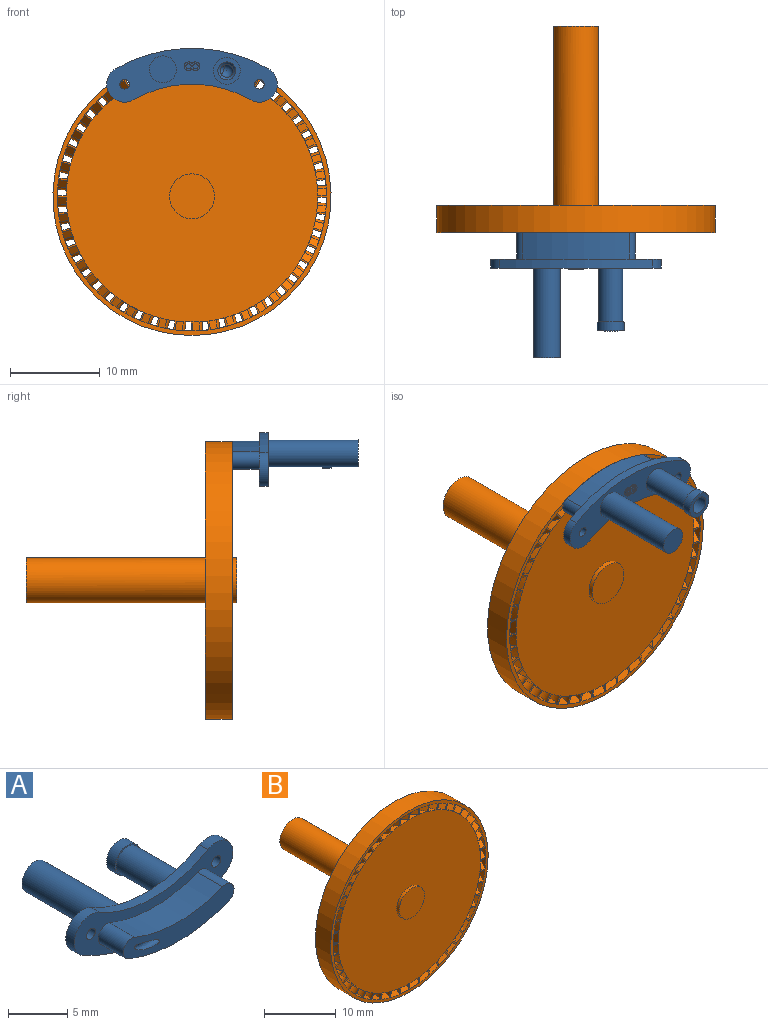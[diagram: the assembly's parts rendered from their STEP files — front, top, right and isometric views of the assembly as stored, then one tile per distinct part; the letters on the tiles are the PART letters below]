
ASSEMBLY  parts=2 mates=1
PART A: 33 faces, bbox 19x14.8x6 mm
  f0: cylinder r=1.5mm len=10mm, axis (0,-1,0), area 94.2mm2, adj f12,f18
  f1: cone r=0.4mm half-angle=45deg, axis (0,1,0), area 2.1mm2, adj f4,f19
  f2: cylinder r=1mm len=3mm, axis (0,1,0), area 9.4mm2, adj f9,f15,f16,f17
  f3: cylinder r=1mm len=3mm, axis (0,1,0), area 9.4mm2, adj f9,f15,f16,f17
  f4: cylinder r=1mm len=6.4mm, axis (0,-1,0), area 40.2mm2, adj f1,f13
  f5: cylinder r=1.5mm len=3mm, axis (0,-1,0), area 9.4mm2, adj f13,f14
  f6: cylinder r=1.35mm len=6mm, axis (0,-1,0), area 50.9mm2, adj f12,f14
  f7: cylinder r=13mm len=13mm, axis (0,-1,0), area 13.6mm2, adj f9,f10,f11,f12
  f8: cylinder r=17mm len=17mm, axis (0,-1,0), area 17.8mm2, adj f9,f10,f11,f12
  f9: plane 19x6.01mm, normal (0,-1,0), area 47.4mm2, adj f2,f3,f7,f8,f10,f11,f15,f16
  f10: cylinder r=2mm len=3.73mm, axis (0,-1,0), area 6.3mm2, adj f7,f8,f9,f12
  f11: cylinder r=2mm len=3.73mm, axis (0,-1,0), area 6.3mm2, adj f7,f8,f9,f12
  f12: plane 19x6.01mm, normal (0,1,0), area 59.4mm2, adj f0,f6,f7,f8,f10,f11,f24,f25
  f13: plane 3x3mm, normal (0,1,0), area 3.9mm2, adj f4,f5
  f14: plane 3x3mm, normal (0,-1,0), area 1.3mm2, adj f5,f6
  f15: cylinder r=16mm len=11.99mm, axis (0,1,0), area 36.9mm2, adj f2,f3,f9,f17
  f16: cylinder r=14mm len=10.49mm, axis (0,1,0), area 32.3mm2, adj f2,f3,f9,f17
  f17: plane 13.24x3.09mm, normal (0,-1,0), area 24.3mm2, adj f2,f3,f15,f16,f21
  f18: plane 3x3mm, normal (0,1,0), area 7.1mm2, adj f0
  f19: cylinder r=0.73mm len=2.27mm, axis (0,-1,0), area 9.9mm2, adj f1,f20,f23
  f20: sphere r=0.73mm, area 2.6mm2, adj f19,f22
  f21: bspline ~8.77x3.01mm, area 17.2mm2, adj f17,f22,f23
  f22: bspline ~1.05x0.66mm, area 0.6mm2, adj f20,f21,f23
  f23: bspline ~0.97x0.73mm, area 0.7mm2, adj f19,f21,f22
  f24: cylinder r=0.53mm len=1.07mm, axis (0,-1,0), area 3.4mm2, adj f9,f12
  f25: cylinder r=0.53mm len=1.07mm, axis (0,-1,0), area 3.4mm2, adj f9,f12
  f26: cylinder r=0.49mm len=0.97mm, axis (0,-1,0), area 0.5mm2, adj f12,f29,f30
  f27: cylinder r=0.29mm len=0.58mm, axis (0,-1,0), area 0.4mm2, adj f30,f32
  f28: cylinder r=0.29mm len=0.58mm, axis (0,-1,0), area 0.4mm2, adj f30,f31
  f29: cylinder r=0.49mm len=0.97mm, axis (0,-1,0), area 0.5mm2, adj f12,f26,f30
  f30: plane 1.75x0.97mm, normal (0,1,0), area 0.9mm2, adj f26,f27,f28,f29
  f31: plane 0.58x0.58mm, normal (0,1,0), area 0.3mm2, adj f28
  f32: plane 0.58x0.58mm, normal (0,1,0), area 0.3mm2, adj f27
PART B: 295 faces, bbox 31x23.5x31 mm
  f0: cylinder r=2.02mm len=3mm, axis (0,0,-1), area 3.4mm2, adj f192,f240,f241,f289
  f1: plane 1.03x0.8mm, normal (-0.71,0.7,0), area 1.1mm2, adj f2,f239,f240,f242
  f2: cylinder r=1mm len=1.4mm, axis (0,0,-1), area 1.6mm2, adj f1,f3,f239,f242
  f3: plane 1.03x0.8mm, normal (-0.72,-0.7,0), area 1.1mm2, adj f2,f239,f241,f242
  f4: cylinder r=2.02mm len=3mm, axis (0.13,0,-0.99), area 3.4mm2, adj f239,f240,f241,f242
  f5: plane 1.12x0.91mm, normal (-0.7,0.7,-0.09), area 1.1mm2, adj f6,f238,f240,f243
  f6: cylinder r=1mm len=1.4mm, axis (0.13,0,-0.99), area 1.6mm2, adj f5,f7,f238,f243
  f7: plane 1.12x0.9mm, normal (-0.71,-0.7,-0.09), area 1.1mm2, adj f6,f238,f241,f243
  f8: cylinder r=2.02mm len=3mm, axis (0.26,0,-0.97), area 3.4mm2, adj f238,f240,f241,f243
  f9: plane 1.2x1.01mm, normal (-0.69,0.7,-0.18), area 1.1mm2, adj f10,f237,f240,f244
  f10: cylinder r=1mm len=1.4mm, axis (0.26,0,-0.97), area 1.6mm2, adj f9,f11,f237,f244
  f11: plane 1.19x1.01mm, normal (-0.69,-0.7,-0.19), area 1.1mm2, adj f10,f237,f241,f244
  f12: cylinder r=2.02mm len=3mm, axis (0.38,0,-0.92), area 3.4mm2, adj f237,f240,f241,f244
  f13: plane 1.25x1.1mm, normal (-0.66,0.7,-0.27), area 1.1mm2, adj f14,f236,f240,f245
  f14: cylinder r=1mm len=1.4mm, axis (0.38,0,-0.92), area 1.6mm2, adj f13,f15,f236,f245
  f15: plane 1.25x1.1mm, normal (-0.66,-0.7,-0.27), area 1.1mm2, adj f14,f236,f241,f245
  f16: cylinder r=2.02mm len=3mm, axis (0.5,0,-0.87), area 3.4mm2, adj f236,f240,f241,f245
  f17: plane 1.28x1.17mm, normal (-0.62,0.7,-0.36), area 1.1mm2, adj f18,f235,f240,f246
  f18: cylinder r=1mm len=1.4mm, axis (0.5,0,-0.87), area 1.6mm2, adj f17,f19,f235,f246
  f19: plane 1.28x1.16mm, normal (-0.62,-0.7,-0.36), area 1.1mm2, adj f18,f235,f241,f246
  f20: cylinder r=2.02mm len=3mm, axis (0.61,0,-0.79), area 3.4mm2, adj f235,f240,f241,f246
  f21: plane 1.29x1.22mm, normal (-0.56,0.7,-0.43), area 1.1mm2, adj f22,f234,f240,f247
  f22: cylinder r=1mm len=1.4mm, axis (0.61,0,-0.79), area 1.6mm2, adj f21,f23,f234,f247
  f23: plane 1.29x1.21mm, normal (-0.57,-0.7,-0.44), area 1.1mm2, adj f22,f234,f241,f247
  f24: cylinder r=2.02mm len=3mm, axis (0.71,0,-0.71), area 3.4mm2, adj f234,f240,f241,f247
  f25: plane 1.28x1.25mm, normal (-0.5,0.7,-0.5), area 1.1mm2, adj f26,f233,f240,f248
  f26: cylinder r=1mm len=1.4mm, axis (0.71,0,-0.71), area 1.6mm2, adj f25,f27,f233,f248
  f27: plane 1.28x1.24mm, normal (-0.51,-0.7,-0.51), area 1.1mm2, adj f26,f233,f241,f248
  f28: cylinder r=2.02mm len=3mm, axis (0.79,0,-0.61), area 3.4mm2, adj f233,f240,f241,f248
  f29: plane 1.25x1.25mm, normal (-0.43,0.7,-0.56), area 1.1mm2, adj f30,f232,f240,f249
  f30: cylinder r=1mm len=1.4mm, axis (0.79,0,-0.61), area 1.6mm2, adj f29,f31,f232,f249
  f31: plane 1.25x1.25mm, normal (-0.44,-0.7,-0.57), area 1.1mm2, adj f30,f232,f241,f249
  f32: cylinder r=2.02mm len=3mm, axis (0.87,0,-0.5), area 3.4mm2, adj f232,f240,f241,f249
  f33: plane 1.24x1.2mm, normal (-0.36,0.7,-0.62), area 1.1mm2, adj f34,f231,f240,f250
  f34: cylinder r=1mm len=1.4mm, axis (0.87,0,-0.5), area 1.6mm2, adj f33,f35,f231,f250
  f35: plane 1.24x1.19mm, normal (-0.36,-0.7,-0.62), area 1.1mm2, adj f34,f231,f241,f250
  f36: cylinder r=2.02mm len=3mm, axis (0.92,0,-0.38), area 3.4mm2, adj f231,f240,f241,f250
  f37: plane 1.2x1.12mm, normal (-0.27,0.7,-0.66), area 1.1mm2, adj f38,f230,f240,f251
  f38: cylinder r=1mm len=1.4mm, axis (0.92,0,-0.38), area 1.6mm2, adj f37,f39,f230,f251
  f39: plane 1.2x1.12mm, normal (-0.27,-0.7,-0.66), area 1.1mm2, adj f38,f230,f241,f251
  f40: cylinder r=2.02mm len=3mm, axis (0.97,0,-0.26), area 3.4mm2, adj f230,f240,f241,f251
  f41: plane 1.15x1.03mm, normal (-0.18,0.7,-0.69), area 1.1mm2, adj f42,f229,f240,f252
  f42: cylinder r=1mm len=1.4mm, axis (0.97,0,-0.26), area 1.6mm2, adj f41,f43,f229,f252
  f43: plane 1.14x1.02mm, normal (-0.19,-0.7,-0.69), area 1.1mm2, adj f42,f229,f241,f252
  f44: cylinder r=2.02mm len=3mm, axis (0.99,0,-0.13), area 3.4mm2, adj f229,f240,f241,f252
  f45: plane 1.07x0.92mm, normal (-0.09,0.7,-0.7), area 1.1mm2, adj f46,f228,f240,f253
  f46: cylinder r=1mm len=1.4mm, axis (0.99,0,-0.13), area 1.6mm2, adj f45,f47,f228,f253
  f47: plane 1.07x0.91mm, normal (-0.09,-0.7,-0.71), area 1.1mm2, adj f46,f228,f241,f253
  f48: cylinder r=2.02mm len=3mm, axis (1,0,0), area 3.4mm2, adj f228,f240,f241,f253
  f49: plane 1.03x0.8mm, normal (0,0.7,-0.71), area 1.1mm2, adj f50,f227,f240,f254
  f50: cylinder r=1mm len=1.4mm, axis (1,0,0), area 1.6mm2, adj f49,f51,f227,f254
  f51: plane 1.03x0.8mm, normal (0,-0.7,-0.72), area 1.1mm2, adj f50,f227,f241,f254
  f52: cylinder r=2.02mm len=3mm, axis (0.99,0,0.13), area 3.4mm2, adj f227,f240,f241,f254
  f53: plane 1.12x0.91mm, normal (0.09,0.7,-0.7), area 1.1mm2, adj f54,f226,f240,f255
  f54: cylinder r=1mm len=1.4mm, axis (0.99,0,0.13), area 1.6mm2, adj f53,f55,f226,f255
  f55: plane 1.12x0.9mm, normal (0.09,-0.7,-0.71), area 1.1mm2, adj f54,f226,f241,f255
  f56: cylinder r=2.02mm len=3mm, axis (0.97,0,0.26), area 3.4mm2, adj f226,f240,f241,f255
  f57: plane 1.2x1.01mm, normal (0.18,0.7,-0.69), area 1.1mm2, adj f58,f225,f240,f256
  f58: cylinder r=1mm len=1.4mm, axis (0.97,0,0.26), area 1.6mm2, adj f57,f59,f225,f256
  f59: plane 1.19x1.01mm, normal (0.19,-0.7,-0.69), area 1.1mm2, adj f58,f225,f241,f256
  f60: cylinder r=2.02mm len=3mm, axis (0.92,0,0.38), area 3.4mm2, adj f225,f240,f241,f256
  f61: plane 1.25x1.1mm, normal (0.27,0.7,-0.66), area 1.1mm2, adj f62,f224,f240,f257
  f62: cylinder r=1mm len=1.4mm, axis (0.92,0,0.38), area 1.6mm2, adj f61,f63,f224,f257
  f63: plane 1.25x1.1mm, normal (0.27,-0.7,-0.66), area 1.1mm2, adj f62,f224,f241,f257
  f64: cylinder r=2.02mm len=3mm, axis (0.87,0,0.5), area 3.4mm2, adj f224,f240,f241,f257
  f65: plane 1.28x1.17mm, normal (0.36,0.7,-0.62), area 1.1mm2, adj f66,f223,f240,f258
  f66: cylinder r=1mm len=1.4mm, axis (0.87,0,0.5), area 1.6mm2, adj f65,f67,f223,f258
  f67: plane 1.28x1.16mm, normal (0.36,-0.7,-0.62), area 1.1mm2, adj f66,f223,f241,f258
  f68: cylinder r=2.02mm len=3mm, axis (0.79,0,0.61), area 3.4mm2, adj f223,f240,f241,f258
  f69: plane 1.29x1.22mm, normal (0.43,0.7,-0.56), area 1.1mm2, adj f70,f222,f240,f259
  f70: cylinder r=1mm len=1.4mm, axis (0.79,0,0.61), area 1.6mm2, adj f69,f71,f222,f259
  f71: plane 1.29x1.21mm, normal (0.44,-0.7,-0.57), area 1.1mm2, adj f70,f222,f241,f259
  f72: cylinder r=2.02mm len=3mm, axis (0.71,0,0.71), area 3.4mm2, adj f222,f240,f241,f259
  f73: plane 1.28x1.25mm, normal (0.5,0.7,-0.5), area 1.1mm2, adj f74,f221,f240,f260
  f74: cylinder r=1mm len=1.4mm, axis (0.71,0,0.71), area 1.6mm2, adj f73,f75,f221,f260
  f75: plane 1.28x1.24mm, normal (0.51,-0.7,-0.51), area 1.1mm2, adj f74,f221,f241,f260
  f76: cylinder r=2.02mm len=3mm, axis (0.61,0,0.79), area 3.4mm2, adj f221,f240,f241,f260
  f77: plane 1.25x1.25mm, normal (0.56,0.7,-0.43), area 1.1mm2, adj f78,f220,f240,f261
  f78: cylinder r=1mm len=1.4mm, axis (0.61,0,0.79), area 1.6mm2, adj f77,f79,f220,f261
  f79: plane 1.25x1.25mm, normal (0.57,-0.7,-0.44), area 1.1mm2, adj f78,f220,f241,f261
  f80: cylinder r=2.02mm len=3mm, axis (0.5,0,0.87), area 3.4mm2, adj f220,f240,f241,f261
  f81: plane 1.24x1.2mm, normal (0.62,0.7,-0.36), area 1.1mm2, adj f82,f219,f240,f262
  f82: cylinder r=1mm len=1.4mm, axis (0.5,0,0.87), area 1.6mm2, adj f81,f83,f219,f262
  f83: plane 1.24x1.19mm, normal (0.62,-0.7,-0.36), area 1.1mm2, adj f82,f219,f241,f262
  f84: cylinder r=2.02mm len=3mm, axis (0.38,0,0.92), area 3.4mm2, adj f219,f240,f241,f262
  f85: plane 1.2x1.12mm, normal (0.66,0.7,-0.27), area 1.1mm2, adj f86,f218,f240,f263
  f86: cylinder r=1mm len=1.4mm, axis (0.38,0,0.92), area 1.6mm2, adj f85,f87,f218,f263
  f87: plane 1.2x1.12mm, normal (0.66,-0.7,-0.27), area 1.1mm2, adj f86,f218,f241,f263
  f88: cylinder r=2.02mm len=3mm, axis (0.26,0,0.97), area 3.4mm2, adj f218,f240,f241,f263
  f89: plane 1.15x1.03mm, normal (0.69,0.7,-0.18), area 1.1mm2, adj f90,f217,f240,f264
  f90: cylinder r=1mm len=1.4mm, axis (0.26,0,0.97), area 1.6mm2, adj f89,f91,f217,f264
  f91: plane 1.14x1.02mm, normal (0.69,-0.7,-0.19), area 1.1mm2, adj f90,f217,f241,f264
  f92: cylinder r=2.02mm len=3mm, axis (0.13,0,0.99), area 3.4mm2, adj f217,f240,f241,f264
  f93: plane 1.07x0.92mm, normal (0.7,0.7,-0.09), area 1.1mm2, adj f94,f216,f240,f265
  f94: cylinder r=1mm len=1.4mm, axis (0.13,0,0.99), area 1.6mm2, adj f93,f95,f216,f265
  f95: plane 1.07x0.91mm, normal (0.71,-0.7,-0.09), area 1.1mm2, adj f94,f216,f241,f265
  f96: cylinder r=2.02mm len=3mm, axis (0,0,1), area 3.4mm2, adj f216,f240,f241,f265
  f97: plane 1.03x0.8mm, normal (0.71,0.7,0), area 1.1mm2, adj f98,f215,f240,f266
  f98: cylinder r=1mm len=1.4mm, axis (0,0,1), area 1.6mm2, adj f97,f99,f215,f266
  f99: plane 1.03x0.8mm, normal (0.72,-0.7,0), area 1.1mm2, adj f98,f215,f241,f266
  f100: cylinder r=2.02mm len=3mm, axis (-0.13,0,0.99), area 3.4mm2, adj f215,f240,f241,f266
  f101: plane 1.12x0.91mm, normal (0.7,0.7,0.09), area 1.1mm2, adj f102,f214,f240,f267
  f102: cylinder r=1mm len=1.4mm, axis (-0.13,0,0.99), area 1.6mm2, adj f101,f103,f214,f267
  f103: plane 1.12x0.9mm, normal (0.71,-0.7,0.09), area 1.1mm2, adj f102,f214,f241,f267
  f104: cylinder r=2.02mm len=3mm, axis (-0.26,0,0.97), area 3.4mm2, adj f214,f240,f241,f267
  f105: plane 1.2x1.01mm, normal (0.69,0.7,0.18), area 1.1mm2, adj f106,f213,f240,f268
  f106: cylinder r=1mm len=1.4mm, axis (-0.26,0,0.97), area 1.6mm2, adj f105,f107,f213,f268
  f107: plane 1.19x1.01mm, normal (0.69,-0.7,0.19), area 1.1mm2, adj f106,f213,f241,f268
  f108: cylinder r=2.02mm len=3mm, axis (-0.38,0,0.92), area 3.4mm2, adj f213,f240,f241,f268
  f109: plane 1.25x1.1mm, normal (0.66,0.7,0.27), area 1.1mm2, adj f110,f212,f240,f269
  f110: cylinder r=1mm len=1.4mm, axis (-0.38,0,0.92), area 1.6mm2, adj f109,f111,f212,f269
  f111: plane 1.25x1.1mm, normal (0.66,-0.7,0.27), area 1.1mm2, adj f110,f212,f241,f269
  f112: cylinder r=2.02mm len=3mm, axis (-0.5,0,0.87), area 3.4mm2, adj f212,f240,f241,f269
  f113: plane 1.28x1.17mm, normal (0.62,0.7,0.36), area 1.1mm2, adj f114,f211,f240,f270
  f114: cylinder r=1mm len=1.4mm, axis (-0.5,0,0.87), area 1.6mm2, adj f113,f115,f211,f270
  f115: plane 1.28x1.16mm, normal (0.62,-0.7,0.36), area 1.1mm2, adj f114,f211,f241,f270
  f116: cylinder r=2.02mm len=3mm, axis (-0.61,0,0.79), area 3.4mm2, adj f211,f240,f241,f270
  f117: plane 1.29x1.22mm, normal (0.56,0.7,0.43), area 1.1mm2, adj f118,f210,f240,f271
  f118: cylinder r=1mm len=1.4mm, axis (-0.61,0,0.79), area 1.6mm2, adj f117,f119,f210,f271
  f119: plane 1.29x1.21mm, normal (0.57,-0.7,0.44), area 1.1mm2, adj f118,f210,f241,f271
  f120: cylinder r=2.02mm len=3mm, axis (-0.71,0,0.71), area 3.4mm2, adj f210,f240,f241,f271
  f121: plane 1.28x1.25mm, normal (0.5,0.7,0.5), area 1.1mm2, adj f122,f209,f240,f272
  f122: cylinder r=1mm len=1.4mm, axis (-0.71,0,0.71), area 1.6mm2, adj f121,f123,f209,f272
  f123: plane 1.28x1.24mm, normal (0.51,-0.7,0.51), area 1.1mm2, adj f122,f209,f241,f272
  f124: cylinder r=2.02mm len=3mm, axis (-0.79,0,0.61), area 3.4mm2, adj f209,f240,f241,f272
  f125: plane 1.25x1.25mm, normal (0.43,0.7,0.56), area 1.1mm2, adj f126,f208,f240,f273
  f126: cylinder r=1mm len=1.4mm, axis (-0.79,0,0.61), area 1.6mm2, adj f125,f127,f208,f273
  f127: plane 1.25x1.25mm, normal (0.44,-0.7,0.57), area 1.1mm2, adj f126,f208,f241,f273
  f128: cylinder r=2.02mm len=3mm, axis (-0.87,0,0.5), area 3.4mm2, adj f208,f240,f241,f273
  f129: plane 1.24x1.2mm, normal (0.36,0.7,0.62), area 1.1mm2, adj f130,f207,f240,f274
  f130: cylinder r=1mm len=1.4mm, axis (-0.87,0,0.5), area 1.6mm2, adj f129,f131,f207,f274
  f131: plane 1.24x1.19mm, normal (0.36,-0.7,0.62), area 1.1mm2, adj f130,f207,f241,f274
  f132: cylinder r=2.02mm len=3mm, axis (-0.92,0,0.38), area 3.4mm2, adj f207,f240,f241,f274
  f133: plane 1.2x1.12mm, normal (0.27,0.7,0.66), area 1.1mm2, adj f134,f206,f240,f275
  f134: cylinder r=1mm len=1.4mm, axis (-0.92,0,0.38), area 1.6mm2, adj f133,f135,f206,f275
  f135: plane 1.2x1.12mm, normal (0.27,-0.7,0.66), area 1.1mm2, adj f134,f206,f241,f275
  f136: cylinder r=2.02mm len=3mm, axis (-0.97,0,0.26), area 3.4mm2, adj f206,f240,f241,f275
  f137: plane 1.15x1.03mm, normal (0.18,0.7,0.69), area 1.1mm2, adj f138,f205,f240,f276
  f138: cylinder r=1mm len=1.4mm, axis (-0.97,0,0.26), area 1.6mm2, adj f137,f139,f205,f276
  f139: plane 1.14x1.02mm, normal (0.19,-0.7,0.69), area 1.1mm2, adj f138,f205,f241,f276
  f140: cylinder r=2.02mm len=3mm, axis (-0.99,0,0.13), area 3.4mm2, adj f205,f240,f241,f276
  f141: plane 1.07x0.92mm, normal (0.09,0.7,0.7), area 1.1mm2, adj f142,f204,f240,f277
  f142: cylinder r=1mm len=1.4mm, axis (-0.99,0,0.13), area 1.6mm2, adj f141,f143,f204,f277
  f143: plane 1.07x0.91mm, normal (0.09,-0.7,0.71), area 1.1mm2, adj f142,f204,f241,f277
  f144: cylinder r=2.02mm len=3mm, axis (-1,0,0), area 3.4mm2, adj f204,f240,f241,f277
  f145: plane 1.03x0.8mm, normal (0,0.7,0.71), area 1.1mm2, adj f146,f203,f240,f278
  f146: cylinder r=1mm len=1.4mm, axis (-1,0,0), area 1.6mm2, adj f145,f147,f203,f278
  f147: plane 1.03x0.8mm, normal (0,-0.7,0.72), area 1.1mm2, adj f146,f203,f241,f278
  f148: cylinder r=2.02mm len=3mm, axis (-0.99,0,-0.13), area 3.4mm2, adj f203,f240,f241,f278
  f149: plane 1.12x0.91mm, normal (-0.09,0.7,0.7), area 1.1mm2, adj f150,f202,f240,f279
  f150: cylinder r=1mm len=1.4mm, axis (-0.99,0,-0.13), area 1.6mm2, adj f149,f151,f202,f279
  f151: plane 1.12x0.9mm, normal (-0.09,-0.7,0.71), area 1.1mm2, adj f150,f202,f241,f279
  f152: cylinder r=2.02mm len=3mm, axis (-0.97,0,-0.26), area 3.4mm2, adj f202,f240,f241,f279
  f153: plane 1.2x1.01mm, normal (-0.18,0.7,0.69), area 1.1mm2, adj f154,f201,f240,f280
  f154: cylinder r=1mm len=1.4mm, axis (-0.97,0,-0.26), area 1.6mm2, adj f153,f155,f201,f280
  f155: plane 1.19x1.01mm, normal (-0.19,-0.7,0.69), area 1.1mm2, adj f154,f201,f241,f280
  f156: cylinder r=2.02mm len=3mm, axis (-0.92,0,-0.38), area 3.4mm2, adj f201,f240,f241,f280
  f157: plane 1.25x1.1mm, normal (-0.27,0.7,0.66), area 1.1mm2, adj f158,f200,f240,f281
  f158: cylinder r=1mm len=1.4mm, axis (-0.92,0,-0.38), area 1.6mm2, adj f157,f159,f200,f281
  f159: plane 1.25x1.1mm, normal (-0.27,-0.7,0.66), area 1.1mm2, adj f158,f200,f241,f281
  f160: cylinder r=2.02mm len=3mm, axis (-0.87,0,-0.5), area 3.4mm2, adj f200,f240,f241,f281
  f161: plane 1.28x1.17mm, normal (-0.36,0.7,0.62), area 1.1mm2, adj f162,f199,f240,f282
  f162: cylinder r=1mm len=1.4mm, axis (-0.87,0,-0.5), area 1.6mm2, adj f161,f163,f199,f282
  f163: plane 1.28x1.16mm, normal (-0.36,-0.7,0.62), area 1.1mm2, adj f162,f199,f241,f282
  f164: cylinder r=2.02mm len=3mm, axis (-0.79,0,-0.61), area 3.4mm2, adj f199,f240,f241,f282
  f165: plane 1.29x1.22mm, normal (-0.43,0.7,0.56), area 1.1mm2, adj f166,f198,f240,f283
  f166: cylinder r=1mm len=1.4mm, axis (-0.79,0,-0.61), area 1.6mm2, adj f165,f167,f198,f283
  f167: plane 1.29x1.21mm, normal (-0.44,-0.7,0.57), area 1.1mm2, adj f166,f198,f241,f283
  f168: cylinder r=2.02mm len=3mm, axis (-0.71,0,-0.71), area 3.4mm2, adj f198,f240,f241,f283
  f169: plane 1.28x1.25mm, normal (-0.5,0.7,0.5), area 1.1mm2, adj f170,f197,f240,f284
  f170: cylinder r=1mm len=1.4mm, axis (-0.71,0,-0.71), area 1.6mm2, adj f169,f171,f197,f284
  f171: plane 1.28x1.24mm, normal (-0.51,-0.7,0.51), area 1.1mm2, adj f170,f197,f241,f284
  f172: cylinder r=2.02mm len=3mm, axis (-0.61,0,-0.79), area 3.4mm2, adj f197,f240,f241,f284
  f173: plane 1.25x1.25mm, normal (-0.56,0.7,0.43), area 1.1mm2, adj f174,f196,f240,f285
  f174: cylinder r=1mm len=1.4mm, axis (-0.61,0,-0.79), area 1.6mm2, adj f173,f175,f196,f285
  f175: plane 1.25x1.25mm, normal (-0.57,-0.7,0.44), area 1.1mm2, adj f174,f196,f241,f285
  f176: cylinder r=2.02mm len=3mm, axis (-0.5,0,-0.87), area 3.4mm2, adj f196,f240,f241,f285
  f177: plane 1.24x1.2mm, normal (-0.62,0.7,0.36), area 1.1mm2, adj f178,f195,f240,f286
  f178: cylinder r=1mm len=1.4mm, axis (-0.5,0,-0.87), area 1.6mm2, adj f177,f179,f195,f286
  f179: plane 1.24x1.19mm, normal (-0.62,-0.7,0.36), area 1.1mm2, adj f178,f195,f241,f286
  f180: cylinder r=2.02mm len=3mm, axis (-0.38,0,-0.92), area 3.4mm2, adj f195,f240,f241,f286
  f181: plane 1.2x1.12mm, normal (-0.66,0.7,0.27), area 1.1mm2, adj f182,f194,f240,f287
  f182: cylinder r=1mm len=1.4mm, axis (-0.38,0,-0.92), area 1.6mm2, adj f181,f183,f194,f287
  f183: plane 1.2x1.12mm, normal (-0.66,-0.7,0.27), area 1.1mm2, adj f182,f194,f241,f287
  f184: cylinder r=2.02mm len=3mm, axis (-0.26,0,-0.97), area 3.4mm2, adj f194,f240,f241,f287
  f185: plane 1.15x1.03mm, normal (-0.69,0.7,0.18), area 1.1mm2, adj f186,f193,f240,f288
  f186: cylinder r=1mm len=1.4mm, axis (-0.26,0,-0.97), area 1.6mm2, adj f185,f187,f193,f288
  f187: plane 1.14x1.02mm, normal (-0.69,-0.7,0.19), area 1.1mm2, adj f186,f193,f241,f288
  f188: cylinder r=2.02mm len=3mm, axis (-0.13,0,-0.99), area 3.4mm2, adj f193,f240,f241,f288
  f189: plane 1.07x0.92mm, normal (-0.7,0.7,0.09), area 1.1mm2, adj f190,f192,f240,f289
  f190: cylinder r=1mm len=1.4mm, axis (-0.13,0,-0.99), area 1.6mm2, adj f189,f191,f192,f289
  f191: plane 1.07x0.91mm, normal (-0.71,-0.7,0.09), area 1.1mm2, adj f190,f192,f241,f289
  f192: cylinder r=14mm len=3mm, axis (0,-1,0), area 4.4mm2, adj f0,f189,f190,f191,f240,f241
  f193: cylinder r=14mm len=3mm, axis (0,-1,0), area 4.4mm2, adj f185,f186,f187,f188,f240,f241
  f194: cylinder r=14mm len=3mm, axis (0,-1,0), area 4.4mm2, adj f181,f182,f183,f184,f240,f241
  f195: cylinder r=14mm len=3mm, axis (0,-1,0), area 4.4mm2, adj f177,f178,f179,f180,f240,f241
  f196: cylinder r=14mm len=3mm, axis (0,-1,0), area 4.4mm2, adj f173,f174,f175,f176,f240,f241
  f197: cylinder r=14mm len=3mm, axis (0,-1,0), area 4.4mm2, adj f169,f170,f171,f172,f240,f241
  f198: cylinder r=14mm len=3mm, axis (0,-1,0), area 4.4mm2, adj f165,f166,f167,f168,f240,f241
  f199: cylinder r=14mm len=3mm, axis (0,-1,0), area 4.4mm2, adj f161,f162,f163,f164,f240,f241
  f200: cylinder r=14mm len=3mm, axis (0,-1,0), area 4.4mm2, adj f157,f158,f159,f160,f240,f241
  f201: cylinder r=14mm len=3mm, axis (0,-1,0), area 4.4mm2, adj f153,f154,f155,f156,f240,f241
  f202: cylinder r=14mm len=3mm, axis (0,-1,0), area 4.4mm2, adj f149,f150,f151,f152,f240,f241
  f203: cylinder r=14mm len=3mm, axis (0,-1,0), area 4.4mm2, adj f145,f146,f147,f148,f240,f241
  f204: cylinder r=14mm len=3mm, axis (0,-1,0), area 4.4mm2, adj f141,f142,f143,f144,f240,f241
  f205: cylinder r=14mm len=3mm, axis (0,-1,0), area 4.4mm2, adj f137,f138,f139,f140,f240,f241
  f206: cylinder r=14mm len=3mm, axis (0,-1,0), area 4.4mm2, adj f133,f134,f135,f136,f240,f241
  f207: cylinder r=14mm len=3mm, axis (0,-1,0), area 4.4mm2, adj f129,f130,f131,f132,f240,f241
  f208: cylinder r=14mm len=3mm, axis (0,-1,0), area 4.4mm2, adj f125,f126,f127,f128,f240,f241
  f209: cylinder r=14mm len=3mm, axis (0,-1,0), area 4.4mm2, adj f121,f122,f123,f124,f240,f241
  f210: cylinder r=14mm len=3mm, axis (0,-1,0), area 4.4mm2, adj f117,f118,f119,f120,f240,f241
  f211: cylinder r=14mm len=3mm, axis (0,-1,0), area 4.4mm2, adj f113,f114,f115,f116,f240,f241
  f212: cylinder r=14mm len=3mm, axis (0,-1,0), area 4.4mm2, adj f109,f110,f111,f112,f240,f241
  f213: cylinder r=14mm len=3mm, axis (0,-1,0), area 4.4mm2, adj f105,f106,f107,f108,f240,f241
  f214: cylinder r=14mm len=3mm, axis (0,-1,0), area 4.4mm2, adj f101,f102,f103,f104,f240,f241
  f215: cylinder r=14mm len=3mm, axis (0,-1,0), area 4.4mm2, adj f97,f98,f99,f100,f240,f241
  f216: cylinder r=14mm len=3mm, axis (0,-1,0), area 4.4mm2, adj f93,f94,f95,f96,f240,f241
  f217: cylinder r=14mm len=3mm, axis (0,-1,0), area 4.4mm2, adj f89,f90,f91,f92,f240,f241
  f218: cylinder r=14mm len=3mm, axis (0,-1,0), area 4.4mm2, adj f85,f86,f87,f88,f240,f241
  f219: cylinder r=14mm len=3mm, axis (0,-1,0), area 4.4mm2, adj f81,f82,f83,f84,f240,f241
  f220: cylinder r=14mm len=3mm, axis (0,-1,0), area 4.4mm2, adj f77,f78,f79,f80,f240,f241
  f221: cylinder r=14mm len=3mm, axis (0,-1,0), area 4.4mm2, adj f73,f74,f75,f76,f240,f241
  f222: cylinder r=14mm len=3mm, axis (0,-1,0), area 4.4mm2, adj f69,f70,f71,f72,f240,f241
  f223: cylinder r=14mm len=3mm, axis (0,-1,0), area 4.4mm2, adj f65,f66,f67,f68,f240,f241
  f224: cylinder r=14mm len=3mm, axis (0,-1,0), area 4.4mm2, adj f61,f62,f63,f64,f240,f241
  f225: cylinder r=14mm len=3mm, axis (0,-1,0), area 4.4mm2, adj f57,f58,f59,f60,f240,f241
  f226: cylinder r=14mm len=3mm, axis (0,-1,0), area 4.4mm2, adj f53,f54,f55,f56,f240,f241
  f227: cylinder r=14mm len=3mm, axis (0,-1,0), area 4.4mm2, adj f49,f50,f51,f52,f240,f241
  f228: cylinder r=14mm len=3mm, axis (0,-1,0), area 4.4mm2, adj f45,f46,f47,f48,f240,f241
  f229: cylinder r=14mm len=3mm, axis (0,-1,0), area 4.4mm2, adj f41,f42,f43,f44,f240,f241
  f230: cylinder r=14mm len=3mm, axis (0,-1,0), area 4.4mm2, adj f37,f38,f39,f40,f240,f241
  f231: cylinder r=14mm len=3mm, axis (0,-1,0), area 4.4mm2, adj f33,f34,f35,f36,f240,f241
  f232: cylinder r=14mm len=3mm, axis (0,-1,0), area 4.4mm2, adj f29,f30,f31,f32,f240,f241
  f233: cylinder r=14mm len=3mm, axis (0,-1,0), area 4.4mm2, adj f25,f26,f27,f28,f240,f241
  f234: cylinder r=14mm len=3mm, axis (0,-1,0), area 4.4mm2, adj f21,f22,f23,f24,f240,f241
  f235: cylinder r=14mm len=3mm, axis (0,-1,0), area 4.4mm2, adj f17,f18,f19,f20,f240,f241
  f236: cylinder r=14mm len=3mm, axis (0,-1,0), area 4.4mm2, adj f13,f14,f15,f16,f240,f241
  f237: cylinder r=14mm len=3mm, axis (0,-1,0), area 4.4mm2, adj f9,f10,f11,f12,f240,f241
  f238: cylinder r=14mm len=3mm, axis (0,-1,0), area 4.4mm2, adj f5,f6,f7,f8,f240,f241
  f239: cylinder r=14mm len=3mm, axis (0,-1,0), area 4.4mm2, adj f1,f2,f3,f4,f240,f241
  f240: plane 31x31mm, normal (0,1,0), area 652.1mm2, adj f0,f1,f4,f5,f8,f9,f12,f13
  f241: plane 31x31mm, normal (0,-1,0), area 652.7mm2, adj f0,f3,f4,f7,f8,f11,f12,f15
  f242: cylinder r=15mm len=3mm, axis (0,-1,0), area 4.7mm2, adj f1,f2,f3,f4,f240,f241
  f243: cylinder r=15mm len=3mm, axis (0,-1,0), area 4.7mm2, adj f5,f6,f7,f8,f240,f241
  f244: cylinder r=15mm len=3mm, axis (0,-1,0), area 4.7mm2, adj f9,f10,f11,f12,f240,f241
  f245: cylinder r=15mm len=3mm, axis (0,-1,0), area 4.7mm2, adj f13,f14,f15,f16,f240,f241
  f246: cylinder r=15mm len=3mm, axis (0,-1,0), area 4.7mm2, adj f17,f18,f19,f20,f240,f241
  f247: cylinder r=15mm len=3mm, axis (0,-1,0), area 4.7mm2, adj f21,f22,f23,f24,f240,f241
  f248: cylinder r=15mm len=3mm, axis (0,-1,0), area 4.7mm2, adj f25,f26,f27,f28,f240,f241
  f249: cylinder r=15mm len=3mm, axis (0,-1,0), area 4.7mm2, adj f29,f30,f31,f32,f240,f241
  f250: cylinder r=15mm len=3mm, axis (0,-1,0), area 4.7mm2, adj f33,f34,f35,f36,f240,f241
  f251: cylinder r=15mm len=3mm, axis (0,-1,0), area 4.7mm2, adj f37,f38,f39,f40,f240,f241
  f252: cylinder r=15mm len=3mm, axis (0,-1,0), area 4.7mm2, adj f41,f42,f43,f44,f240,f241
  f253: cylinder r=15mm len=3mm, axis (0,-1,0), area 4.7mm2, adj f45,f46,f47,f48,f240,f241
  f254: cylinder r=15mm len=3mm, axis (0,-1,0), area 4.7mm2, adj f49,f50,f51,f52,f240,f241
  f255: cylinder r=15mm len=3mm, axis (0,-1,0), area 4.7mm2, adj f53,f54,f55,f56,f240,f241
  f256: cylinder r=15mm len=3mm, axis (0,-1,0), area 4.7mm2, adj f57,f58,f59,f60,f240,f241
  f257: cylinder r=15mm len=3mm, axis (0,-1,0), area 4.7mm2, adj f61,f62,f63,f64,f240,f241
  f258: cylinder r=15mm len=3mm, axis (0,-1,0), area 4.7mm2, adj f65,f66,f67,f68,f240,f241
  f259: cylinder r=15mm len=3mm, axis (0,-1,0), area 4.7mm2, adj f69,f70,f71,f72,f240,f241
  f260: cylinder r=15mm len=3mm, axis (0,-1,0), area 4.7mm2, adj f73,f74,f75,f76,f240,f241
  f261: cylinder r=15mm len=3mm, axis (0,-1,0), area 4.7mm2, adj f77,f78,f79,f80,f240,f241
  f262: cylinder r=15mm len=3mm, axis (0,-1,0), area 4.7mm2, adj f81,f82,f83,f84,f240,f241
  f263: cylinder r=15mm len=3mm, axis (0,-1,0), area 4.7mm2, adj f85,f86,f87,f88,f240,f241
  f264: cylinder r=15mm len=3mm, axis (0,-1,0), area 4.7mm2, adj f89,f90,f91,f92,f240,f241
  f265: cylinder r=15mm len=3mm, axis (0,-1,0), area 4.7mm2, adj f93,f94,f95,f96,f240,f241
  f266: cylinder r=15mm len=3mm, axis (0,-1,0), area 4.7mm2, adj f97,f98,f99,f100,f240,f241
  f267: cylinder r=15mm len=3mm, axis (0,-1,0), area 4.7mm2, adj f101,f102,f103,f104,f240,f241
  f268: cylinder r=15mm len=3mm, axis (0,-1,0), area 4.7mm2, adj f105,f106,f107,f108,f240,f241
  f269: cylinder r=15mm len=3mm, axis (0,-1,0), area 4.7mm2, adj f109,f110,f111,f112,f240,f241
  f270: cylinder r=15mm len=3mm, axis (0,-1,0), area 4.7mm2, adj f113,f114,f115,f116,f240,f241
  f271: cylinder r=15mm len=3mm, axis (0,-1,0), area 4.7mm2, adj f117,f118,f119,f120,f240,f241
  f272: cylinder r=15mm len=3mm, axis (0,-1,0), area 4.7mm2, adj f121,f122,f123,f124,f240,f241
  f273: cylinder r=15mm len=3mm, axis (0,-1,0), area 4.7mm2, adj f125,f126,f127,f128,f240,f241
  f274: cylinder r=15mm len=3mm, axis (0,-1,0), area 4.7mm2, adj f129,f130,f131,f132,f240,f241
  f275: cylinder r=15mm len=3mm, axis (0,-1,0), area 4.7mm2, adj f133,f134,f135,f136,f240,f241
  f276: cylinder r=15mm len=3mm, axis (0,-1,0), area 4.7mm2, adj f137,f138,f139,f140,f240,f241
  f277: cylinder r=15mm len=3mm, axis (0,-1,0), area 4.7mm2, adj f141,f142,f143,f144,f240,f241
  f278: cylinder r=15mm len=3mm, axis (0,-1,0), area 4.7mm2, adj f145,f146,f147,f148,f240,f241
  f279: cylinder r=15mm len=3mm, axis (0,-1,0), area 4.7mm2, adj f149,f150,f151,f152,f240,f241
  f280: cylinder r=15mm len=3mm, axis (0,-1,0), area 4.7mm2, adj f153,f154,f155,f156,f240,f241
  f281: cylinder r=15mm len=3mm, axis (0,-1,0), area 4.7mm2, adj f157,f158,f159,f160,f240,f241
  f282: cylinder r=15mm len=3mm, axis (0,-1,0), area 4.7mm2, adj f161,f162,f163,f164,f240,f241
  f283: cylinder r=15mm len=3mm, axis (0,-1,0), area 4.7mm2, adj f165,f166,f167,f168,f240,f241
  f284: cylinder r=15mm len=3mm, axis (0,-1,0), area 4.7mm2, adj f169,f170,f171,f172,f240,f241
  f285: cylinder r=15mm len=3mm, axis (0,-1,0), area 4.7mm2, adj f173,f174,f175,f176,f240,f241
  f286: cylinder r=15mm len=3mm, axis (0,-1,0), area 4.7mm2, adj f177,f178,f179,f180,f240,f241
  f287: cylinder r=15mm len=3mm, axis (0,-1,0), area 4.7mm2, adj f181,f182,f183,f184,f240,f241
  f288: cylinder r=15mm len=3mm, axis (0,-1,0), area 4.7mm2, adj f185,f186,f187,f188,f240,f241
  f289: cylinder r=15mm len=3mm, axis (0,-1,0), area 4.7mm2, adj f0,f189,f190,f191,f240,f241
  f290: cylinder r=15.5mm len=31mm, axis (0,-1,0), area 292.2mm2, adj f240,f241
  f291: cylinder r=2.5mm len=5mm, axis (0,1,0), area 7.9mm2, adj f241,f292
  f292: plane 5x5mm, normal (0,-1,0), area 19.6mm2, adj f291
  f293: cylinder r=2.5mm len=20mm, axis (0,-1,0), area 314.2mm2, adj f240,f294
  f294: plane 5x5mm, normal (0,1,0), area 19.6mm2, adj f293
PLACE A rot(axis=(1,0,0),180deg) t=(0,-2.93,-0.07)mm
PLACE B at identity
MATE fastened B.f290 <-> A.f17  axis (0,-1,0) through (0,0,0)mm
